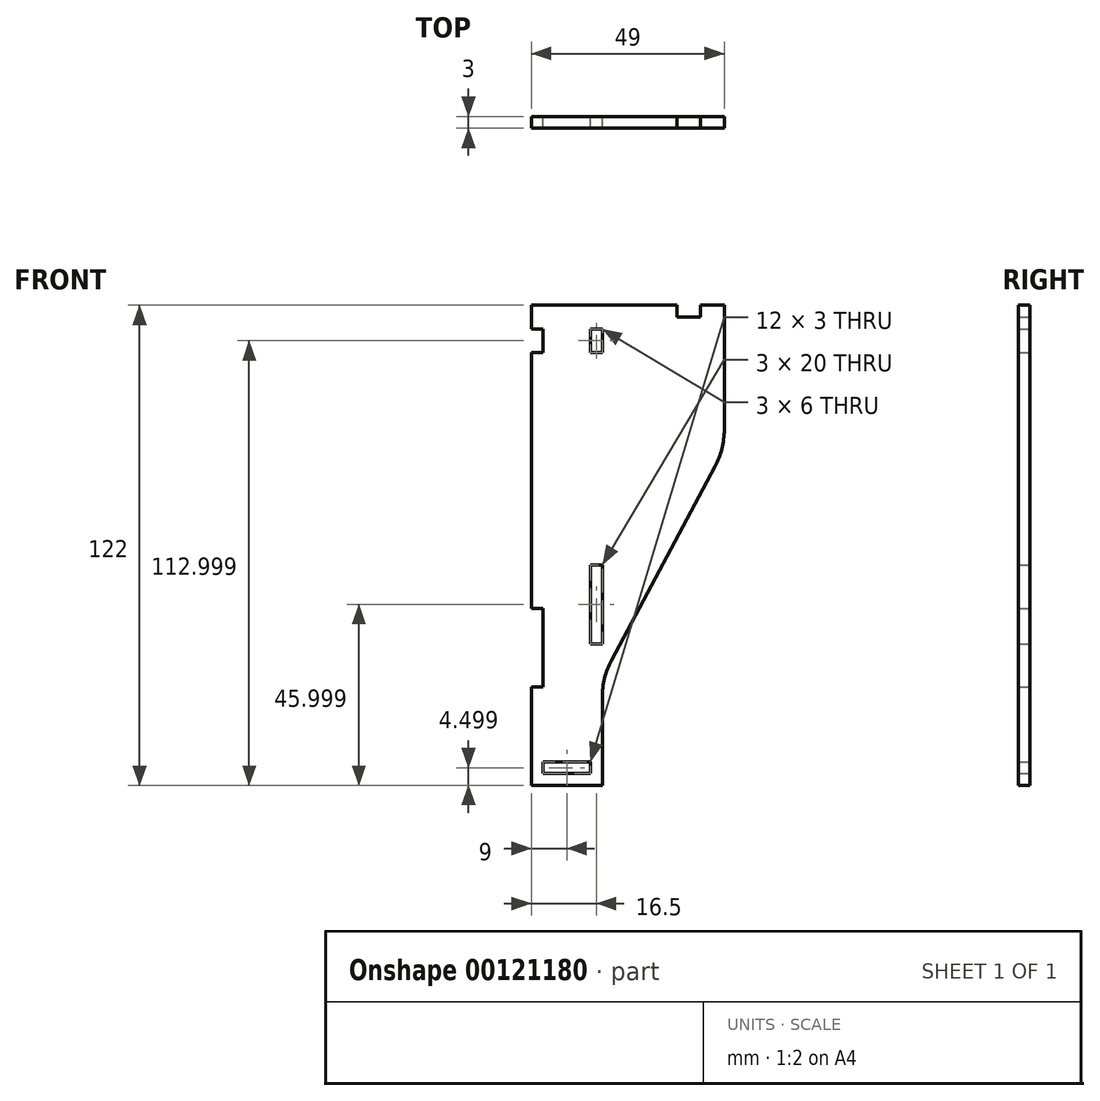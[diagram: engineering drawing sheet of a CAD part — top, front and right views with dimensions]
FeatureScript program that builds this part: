
annotation { "Feature Type Name" : "Feature", "Feature Type Description" : "" }
export const myFeature = defineFeature(function(context is Context, id is Id, definition is map)
    precondition{}
    {
        {
            var Q0;
            Q0=qCreatedBy(makeId("Front.planeOp"),FACE);
            var sketch = newSketch(context, id + "F0", { "sketchPlane" : qUnion([Q0])});
            skLineSegment(sketch, "E0", {"start": v(-184.2, 90.2) * mm, "end": v(-147.2, 90.2) * mm});
            skLineSegment(sketch, "E1", {"start": v(-135.2, 90.2) * mm, "end": v(-135.2, 58.61) * mm});
            skLineSegment(sketch, "E2", {"start": v(-137.56, 49.19) * mm, "end": v(-163.84, 0) * mm});
            skLineSegment(sketch, "E3", {"start": v(-166.2, -9.43) * mm, "end": v(-166.2, -31.8) * mm});
            skLineSegment(sketch, "E4", {"start": v(-184.2, -31.8) * mm, "end": v(-184.2, -6.8) * mm});
            skPoint(sketch, "E5.visualSharp", {"position": v(-135.2, 53.6) * mm});
            skArc(sketch, "E5.filletArc", {"start": v(-168.45, 43.63) * mm, "mid": v(-146.98, 40.38) * mm, "end": v(-135.2, 58.61) * mm, "construction": true});
            skPoint(sketch, "E6.visualSharp", {"position": v(-137.56, 49.19) * mm});
            skArc(sketch, "E6.filletArc", {"start": v(-137.56, 49.19) * mm, "mid": v(-135.8, 53.75) * mm, "end": v(-135.2, 58.61) * mm});
            skPoint(sketch, "E7.visualSharp", {"position": v(-166.2, -4.42) * mm});
            skArc(sketch, "E7.filletArc", {"start": v(-163.84, 0) * mm, "mid": v(-165.6, -4.57) * mm, "end": v(-166.2, -9.43) * mm});
            skLineSegment(sketch, "E8.0", {"start": v(-166.2, -31.8) * mm, "end": v(-184.2, -31.8) * mm});
            skLineSegment(sketch, "E9.bottom", {"start": v(-181.2, -25.8) * mm, "end": v(-169.2, -25.8) * mm});
            skLineSegment(sketch, "E9.top", {"start": v(-181.2, -28.8) * mm, "end": v(-169.2, -28.8) * mm});
            skLineSegment(sketch, "E9.left", {"start": v(-181.2, -25.8) * mm, "end": v(-181.2, -28.8) * mm});
            skLineSegment(sketch, "E9.right", {"start": v(-169.2, -25.8) * mm, "end": v(-169.2, -28.8) * mm});
            skLineSegment(sketch, "E10", {"start": v(-181.2, 84.2) * mm, "end": v(-181.2, 78.2) * mm});
            skLineSegment(sketch, "E11", {"start": v(-184.2, 84.2) * mm, "end": v(-181.2, 84.2) * mm});
            skLineSegment(sketch, "E12", {"start": v(-181.2, 78.2) * mm, "end": v(-184.2, 78.2) * mm});
            skLineSegment(sketch, "E13", {"start": v(-184.2, 84.2) * mm, "end": v(-184.2, 90.2) * mm});
            skLineSegment(sketch, "E14", {"start": v(-184.2, 13.2) * mm, "end": v(-181.2, 13.2) * mm});
            skLineSegment(sketch, "E15", {"start": v(-181.2, -6.8) * mm, "end": v(-184.2, -6.8) * mm});
            skLineSegment(sketch, "E16", {"start": v(-184.2, 13.2) * mm, "end": v(-184.2, 78.2) * mm});
            skLineSegment(sketch, "E17", {"start": v(-181.2, 13.2) * mm, "end": v(-181.2, -6.8) * mm});
            skLineSegment(sketch, "E18.bottom", {"start": v(-166.2, 4.2) * mm, "end": v(-169.2, 4.2) * mm});
            skLineSegment(sketch, "E18.top", {"start": v(-166.2, 24.2) * mm, "end": v(-169.2, 24.2) * mm});
            skLineSegment(sketch, "E18.left", {"start": v(-166.2, 4.2) * mm, "end": v(-166.2, 24.2) * mm});
            skLineSegment(sketch, "E18.right", {"start": v(-169.2, 4.2) * mm, "end": v(-169.2, 24.2) * mm});
            skLineSegment(sketch, "E19.bottom", {"start": v(-169.2, 84.2) * mm, "end": v(-166.2, 84.2) * mm});
            skLineSegment(sketch, "E19.top", {"start": v(-169.2, 78.2) * mm, "end": v(-166.2, 78.2) * mm});
            skLineSegment(sketch, "E19.left", {"start": v(-169.2, 84.2) * mm, "end": v(-169.2, 78.2) * mm});
            skLineSegment(sketch, "E19.right", {"start": v(-166.2, 84.2) * mm, "end": v(-166.2, 78.2) * mm});
            skPoint(sketch, "E20", {"position": v(-174.33, 64.43) * mm});
            skLineSegment(sketch, "E21.bottom", {"start": v(-147.2, 87.2) * mm, "end": v(-141.2, 87.2) * mm});
            skLineSegment(sketch, "E21.left", {"start": v(-147.2, 87.2) * mm, "end": v(-147.2, 90.2) * mm});
            skLineSegment(sketch, "E21.right", {"start": v(-141.2, 87.2) * mm, "end": v(-141.2, 90.2) * mm});
            skLineSegment(sketch, "E22", {"start": v(-141.2, 90.2) * mm, "end": v(-135.2, 90.2) * mm});
            skLineSegment(sketch, "E23", {"start": v(-181.2, -31.8) * mm, "end": v(-181.2, 90.2) * mm, "construction": true});
            skArc(sketch, "E24", {"start": v(-135.2, 58.61) * mm, "mid": v(-163.42, 76.84) * mm, "end": v(-168.45, 43.63) * mm, "construction": true});
            skSolve(sketch);
        }
        {
            var Q0;
            Q0 = qSketchRegion(id + "F0", true);
            extrude(context, id + "F1", {"entities" : qUnion([Q0]), "endBound" : BoundingType.SYMMETRIC, "depth" : 3 * mm});
        }
        {
            var Q0;
            Q0=makeQuery(id+"F0.imprint","IMPRINT",FACE,{"disambiguationData":[TD([[makeQuery(id+"F0.imprint","IMPRINT",EDGE,{"derivedFrom":sQuery(id+"F0.wireOp",EDGE,"E9.bottom")}),-1.0]])]});
            extrude(context, id + "F2", {"entities" : qUnion([Q0]), "operationType" : NewBodyOperationType.REMOVE, "endBound" : BoundingType.SYMMETRIC, "oppositeDirection" : true, "depth" : 3 * mm});
        }
    });
